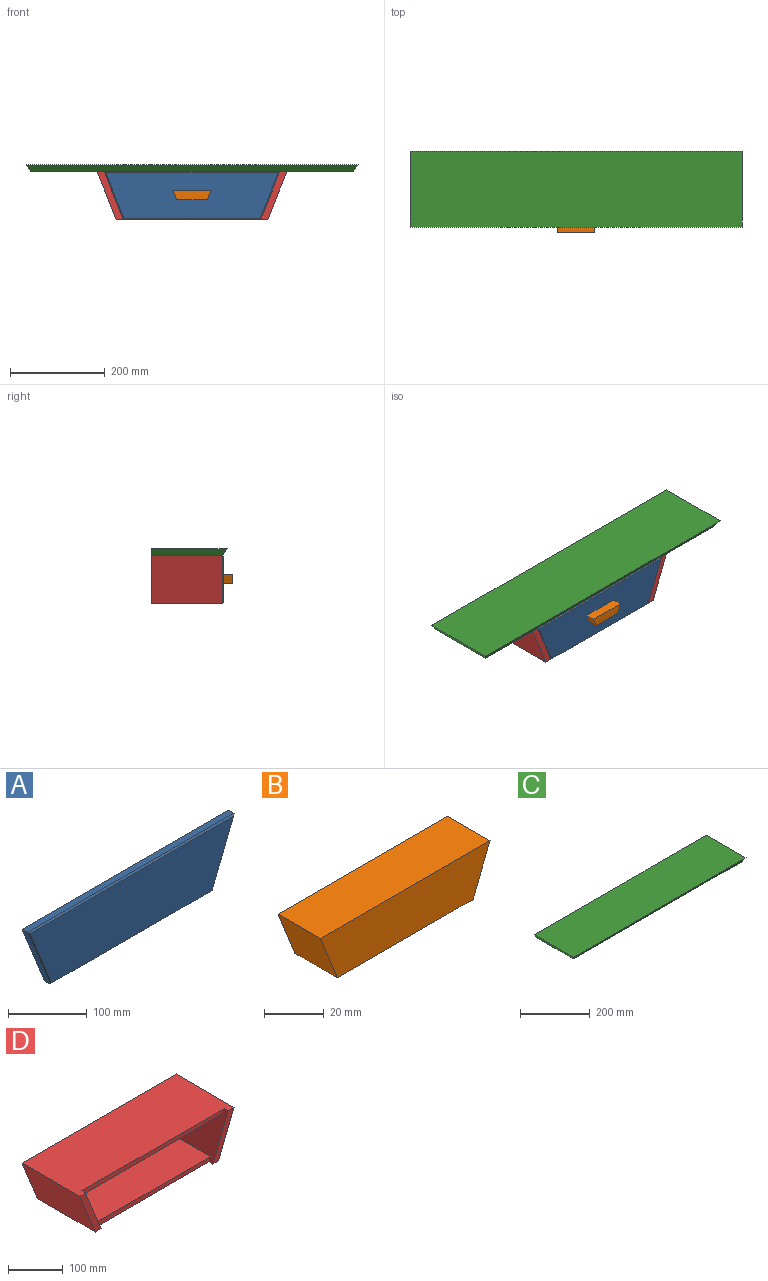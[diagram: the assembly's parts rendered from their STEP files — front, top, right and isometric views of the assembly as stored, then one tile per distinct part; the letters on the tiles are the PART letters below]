
ASSEMBLY  parts=4 mates=3
PART A: 10 faces, bbox 370x12x100 mm
  f0: plane 370x10mm, normal (0,0,1), area 3700mm2, adj f1,f3,f5,f6
  f1: plane 100x40mm, normal (-0.93,0,-0.37), area 1077mm2, adj f0,f2,f5,f7
  f2: plane 290x10mm, normal (0,0,-1), area 2900mm2, adj f1,f3,f5,f9
  f3: plane 100x40mm, normal (0.93,0,-0.37), area 1077mm2, adj f0,f2,f5,f8
  f4: plane 364.09x96mm, normal (0,-1,0), area 31266.4mm2, adj f6,f7,f8,f9
  f5: plane 370x100mm, normal (0,1,0), area 33000mm2, adj f0,f1,f2,f3
  f6: plane 370x2mm, normal (0,-0.71,0.71), area 1038.2mm2, adj f0,f4,f7,f8
  f7: plane 100x41.35mm, normal (-0.66,-0.71,-0.26), area 298.5mm2, adj f1,f4,f6,f9
  f8: plane 100x41.35mm, normal (0.66,-0.71,-0.26), area 298.5mm2, adj f3,f4,f6,f9
  f9: plane 290x2mm, normal (0,-0.71,-0.71), area 816.4mm2, adj f2,f4,f7,f8
PART B: 6 faces, bbox 80x20x20 mm
  f0: plane 64x20mm, normal (0,0,-1), area 1280mm2, adj f2,f3,f4,f5
  f1: plane 80x20mm, normal (0,0,1), area 1600mm2, adj f2,f3,f4,f5
  f2: plane 80x20mm, normal (0,-1,0), area 1440mm2, adj f0,f1,f4,f5
  f3: plane 80x20mm, normal (0,1,0), area 1440mm2, adj f0,f1,f4,f5
  f4: plane 20x20mm, normal (-0.93,0,-0.37), area 430.8mm2, adj f0,f1,f2,f3
  f5: plane 20x20mm, normal (0.93,0,-0.37), area 430.8mm2, adj f0,f1,f2,f3
PART C: 6 faces, bbox 700x160x15 mm
  f0: plane 700x15mm, normal (0,1,0), area 10350mm2, adj f1,f2,f3,f5
  f1: plane 700x160mm, normal (0,0,1), area 112000mm2, adj f0,f3,f4,f5
  f2: plane 680x150mm, normal (0,0,-1), area 102000mm2, adj f0,f3,f4,f5
  f3: plane 160x15mm, normal (0.83,0,-0.55), area 2794.3mm2, adj f0,f1,f2,f4
  f4: plane 700x15mm, normal (0,-0.83,-0.55), area 12439.2mm2, adj f1,f2,f3,f5
  f5: plane 160x15mm, normal (-0.83,0,-0.55), area 2794.3mm2, adj f0,f1,f2,f4
PART D: 14 faces, bbox 400x150x100 mm
  f0: plane 140x100mm, normal (0.93,0,0.37), area 12278.2mm2, adj f1,f4,f5,f6,f10,f11,f12,f13
  f1: plane 362x80mm, normal (0,-1,0), area 26400mm2, adj f0,f2,f10,f12
  f2: plane 140x100mm, normal (-0.93,0,0.37), area 12278.2mm2, adj f1,f3,f4,f5,f10,f11,f12,f13
  f3: plane 100x55mm, normal (0,-1,0), area 1500mm2, adj f2,f4,f5,f9
  f4: plane 320x150mm, normal (0,0,-1), area 45100mm2, adj f0,f2,f3,f6,f7,f8,f9,f11
  f5: plane 400x150mm, normal (0,0,1), area 56300mm2, adj f0,f2,f3,f6,f7,f8,f9,f13
  f6: plane 100x55mm, normal (0,-1,0), area 1500mm2, adj f0,f4,f5,f8
  f7: plane 400x100mm, normal (0,1,0), area 36000mm2, adj f4,f5,f8,f9
  f8: plane 150x100mm, normal (-0.93,0,-0.37), area 16155.5mm2, adj f4,f5,f6,f7
  f9: plane 150x100mm, normal (0.93,0,-0.37), area 16155.5mm2, adj f3,f4,f5,f7
  f10: plane 298x130mm, normal (0,0,1), area 38740mm2, adj f0,f1,f2,f11
  f11: plane 298x10mm, normal (0,-1,0), area 2940mm2, adj f0,f2,f4,f10
  f12: plane 362x130mm, normal (0,0,-1), area 47060mm2, adj f0,f1,f2,f13
  f13: plane 370x10mm, normal (0,-1,0), area 3660mm2, adj f0,f2,f5,f12
PLACE A t=(143.01,-252.83,-68.46)mm
PLACE B t=(143.01,-264.83,-16.94)mm
PLACE C t=(143.01,-192.83,31.54)mm
PLACE D t=(143.01,-112.83,-18.46)mm
MATE fastened A.f4 <-> B.f3  axis (0,-1,0) through (143.01,-264.83,-16.57)mm
MATE fastened D.f11 <-> A.f5  axis (0,-1,0) through (143.01,-252.83,-68.46)mm
MATE fastened D.f5 <-> C.f2  axis (0,0,1) through (143.01,-112.83,31.54)mm
